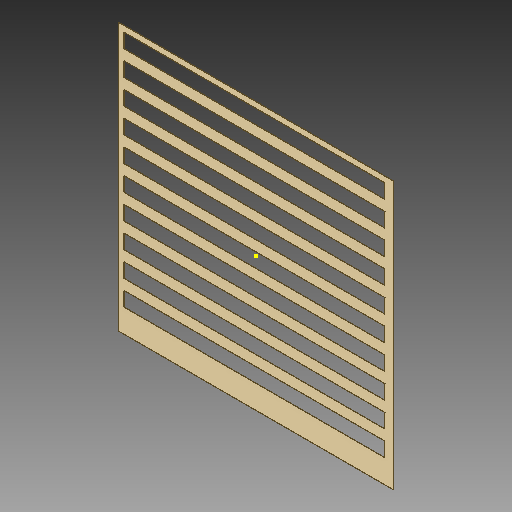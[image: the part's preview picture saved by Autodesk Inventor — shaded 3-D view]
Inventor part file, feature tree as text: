
AUTODESK INVENTOR PART (.ipt)
format: ipt  version: 2018 (Build 220112000, 112)  size: 150,528 bytes
history: native  units: in
note: dims shown in document units (in); Inventor stores cm internally (conversion verified against a paired STEP export)
features: sketch x2, extrude x2
ambient origin geometry x8: Origin, YZ Plane, XZ Plane, XY Plane, X Axis, Y Axis, Z Axis, Center Point
bodies: Solid1 (feature_tree)
feature tree (4):
  sketch  "Sketch1"  dims[d0=730.0in d1=710.0in]
  extrude  "Extrusion1"  Depth=710.0in
  extrude  "Extrusion2"  Depth=1.0in TaperAngle=0.0deg
  sketch  "Sketch3"  dims[d2=240.0in d3=1.0in d4=0.0in d5=3.937in d7=66.0in d8=0.3937in d10=1.0in d12=1.0in d13=0.0in]
